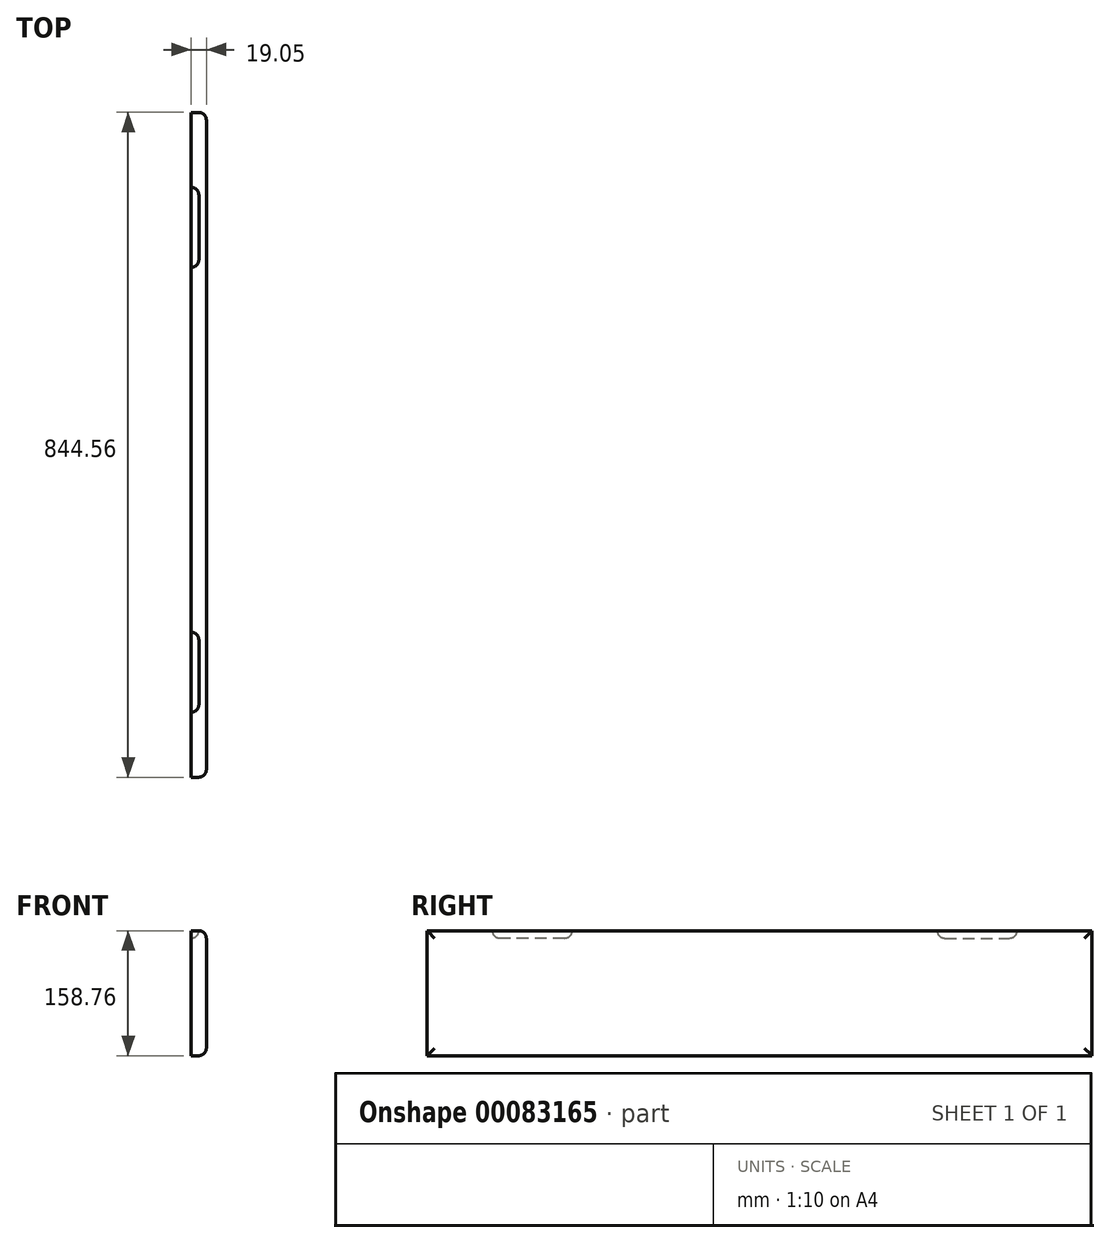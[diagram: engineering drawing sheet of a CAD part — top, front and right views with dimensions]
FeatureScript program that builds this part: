
annotation { "Feature Type Name" : "Feature", "Feature Type Description" : "" }
export const myFeature = defineFeature(function(context is Context, id is Id, definition is map)
    precondition{}
    {
        {
            var Q0;
            Q0=qCreatedBy(makeId("Right.planeOp"),FACE);
            var sketch = newSketch(context, id + "F0", { "sketchPlane" : qUnion([Q0])});
            skLineSegment(sketch, "E0.bottom", {"start": v(422.28, 79.38) * mm, "end": v(-422.28, 79.37) * mm});
            skLineSegment(sketch, "E0.top", {"start": v(422.28, -79.37) * mm, "end": v(-422.28, -79.38) * mm});
            skLineSegment(sketch, "E0.left", {"start": v(422.28, 79.38) * mm, "end": v(422.28, -79.37) * mm});
            skLineSegment(sketch, "E0.right", {"start": v(-422.28, 79.37) * mm, "end": v(-422.28, -79.38) * mm});
            skPoint(sketch, "E0.middle", {"position": v(0, 0) * mm});
            skSolve(sketch);
        }
        {
            var Q0;
            Q0=makeQuery(id+"F0.imprint","IMPRINT",FACE,{"disambiguationData":[TD([[makeQuery(id+"F0.imprint","IMPRINT",EDGE,{"derivedFrom":sQuery(id+"F0.wireOp",EDGE,"E0.bottom")}),1.0]])]});
            extrude(context, id + "F1", {"entities" : qUnion([Q0]), "depth" : 19.05 * mm});
        }
        {
            var Q0;
            Q0=makeQuery(id+"F1.opExtrude","SWEPT_FACE",FACE,{"disambiguationData":[OSD([sQuery(id+"F0.wireOp",EDGE,"E0.right")])]});
            cPlane(context, id + "F2", {"entities" : qUnion([Q0]), "cplaneType" : CPlaneType.OFFSET, "offset" : 82.55 * mm, "oppositeDirection" : true, "width" : 152.4 * mm, "height" : 152.4 * mm});
        }
        {
            var Q0;
            Q0=qCreatedBy(id+"F2.planeOp",FACE);
            var sketch = newSketch(context, id + "F3", { "sketchPlane" : qUnion([Q0])});
            skCircle(sketch, "E1", {"center": v(0, 79.38) * mm, "radius": 9.53 * mm});
            skSolve(sketch);
        }
        {
            var Q0;
            Q0=makeQuery(id+"F3.imprint","IMPRINT",FACE,{"disambiguationData":[TD([[makeQuery(id+"F3.imprint","IMPRINT",EDGE,{"derivedFrom":sQuery(id+"F3.wireOp",EDGE,"E1")}),1.0]])]});
            extrude(context, id + "F4", {"entities" : qUnion([Q0]), "operationType" : NewBodyOperationType.REMOVE, "oppositeDirection" : true, "depth" : 101.6 * mm});
        }
        {
            var Q0;
            Q0=makeQuery(id+"F4.boolean.opBoolean","COPY",EDGE,{"derivedFrom":makeQuery(id+"F4.opExtrude","CAP_EDGE",EDGE,{"disambiguationData":[OSD([sQuery(id+"F3.wireOp",EDGE,"E1")])],"isStart":true})});
            var Q1;
            Q1=makeQuery(id+"F4.boolean.opBoolean","COPY",EDGE,{"derivedFrom":makeQuery(id+"F4.opExtrude","CAP_EDGE",EDGE,{"disambiguationData":[OSD([sQuery(id+"F3.wireOp",EDGE,"E1")])],"isStart":false})});
            fillet(context, id + "F5", {"entities" : qUnion([Q0, Q1]), "radius" : 9.52 * mm, "tangentPropagation" : true, "allowEdgeOverflow" : false});
        }
        {
            var Q0;
            Q0=makeQuery(id+"F1.opExtrude","SWEPT_FACE",FACE,{"disambiguationData":[OSD([sQuery(id+"F0.wireOp",EDGE,"E0.left")])]});
            cPlane(context, id + "F6", {"entities" : qUnion([Q0]), "cplaneType" : CPlaneType.OFFSET, "offset" : 95.25 * mm, "oppositeDirection" : true, "width" : 152.4 * mm, "height" : 152.4 * mm});
        }
        {
            var Q0;
            Q0=qCreatedBy(id+"F6.planeOp",FACE);
            var sketch = newSketch(context, id + "F7", { "sketchPlane" : qUnion([Q0])});
            skCircle(sketch, "E2", {"center": v(0, 79.37) * mm, "radius": 9.53 * mm});
            skSolve(sketch);
        }
        {
            var Q0;
            Q0=makeQuery(id+"F7.imprint","IMPRINT",FACE,{"disambiguationData":[TD([[makeQuery(id+"F7.imprint","IMPRINT",EDGE,{"derivedFrom":sQuery(id+"F7.wireOp",EDGE,"E2")}),1.0]])]});
            extrude(context, id + "F8", {"entities" : qUnion([Q0]), "operationType" : NewBodyOperationType.REMOVE, "oppositeDirection" : true, "depth" : 101.6 * mm});
        }
        {
            var Q0;
            Q0=makeQuery(id+"F8.boolean.opBoolean","COPY",EDGE,{"derivedFrom":makeQuery(id+"F8.opExtrude","CAP_EDGE",EDGE,{"disambiguationData":[OSD([sQuery(id+"F7.wireOp",EDGE,"E2")])],"isStart":false})});
            var Q1;
            Q1=makeQuery(id+"F8.boolean.opBoolean","COPY",EDGE,{"derivedFrom":makeQuery(id+"F8.opExtrude","CAP_EDGE",EDGE,{"disambiguationData":[OSD([sQuery(id+"F7.wireOp",EDGE,"E2")])],"isStart":true})});
            fillet(context, id + "F9", {"entities" : qUnion([Q0, Q1]), "radius" : 9.52 * mm, "tangentPropagation" : true, "allowEdgeOverflow" : false});
        }
        {
            var Q0;
            Q0=makeQuery(id+"F1.opExtrude","CAP_EDGE",EDGE,{"disambiguationData":[OSD([sQuery(id+"F0.wireOp",EDGE,"E0.right")])],"isStart":false});
            var Q1;
            Q1=makeQuery(id+"F1.opExtrude","CAP_EDGE",EDGE,{"disambiguationData":[OSD([sQuery(id+"F0.wireOp",EDGE,"E0.bottom")])],"isStart":false});
            var Q2;
            Q2=makeQuery(id+"F1.opExtrude","CAP_EDGE",EDGE,{"disambiguationData":[OSD([sQuery(id+"F0.wireOp",EDGE,"E0.left")])],"isStart":false});
            var Q3;
            Q3=makeQuery(id+"F1.opExtrude","CAP_EDGE",EDGE,{"disambiguationData":[OSD([sQuery(id+"F0.wireOp",EDGE,"E0.top")])],"isStart":false});
            fillet(context, id + "F10", {"entities" : qUnion([Q0, Q1, Q2, Q3]), "radius" : 9.52 * mm, "tangentPropagation" : true, "allowEdgeOverflow" : false});
        }
    });
